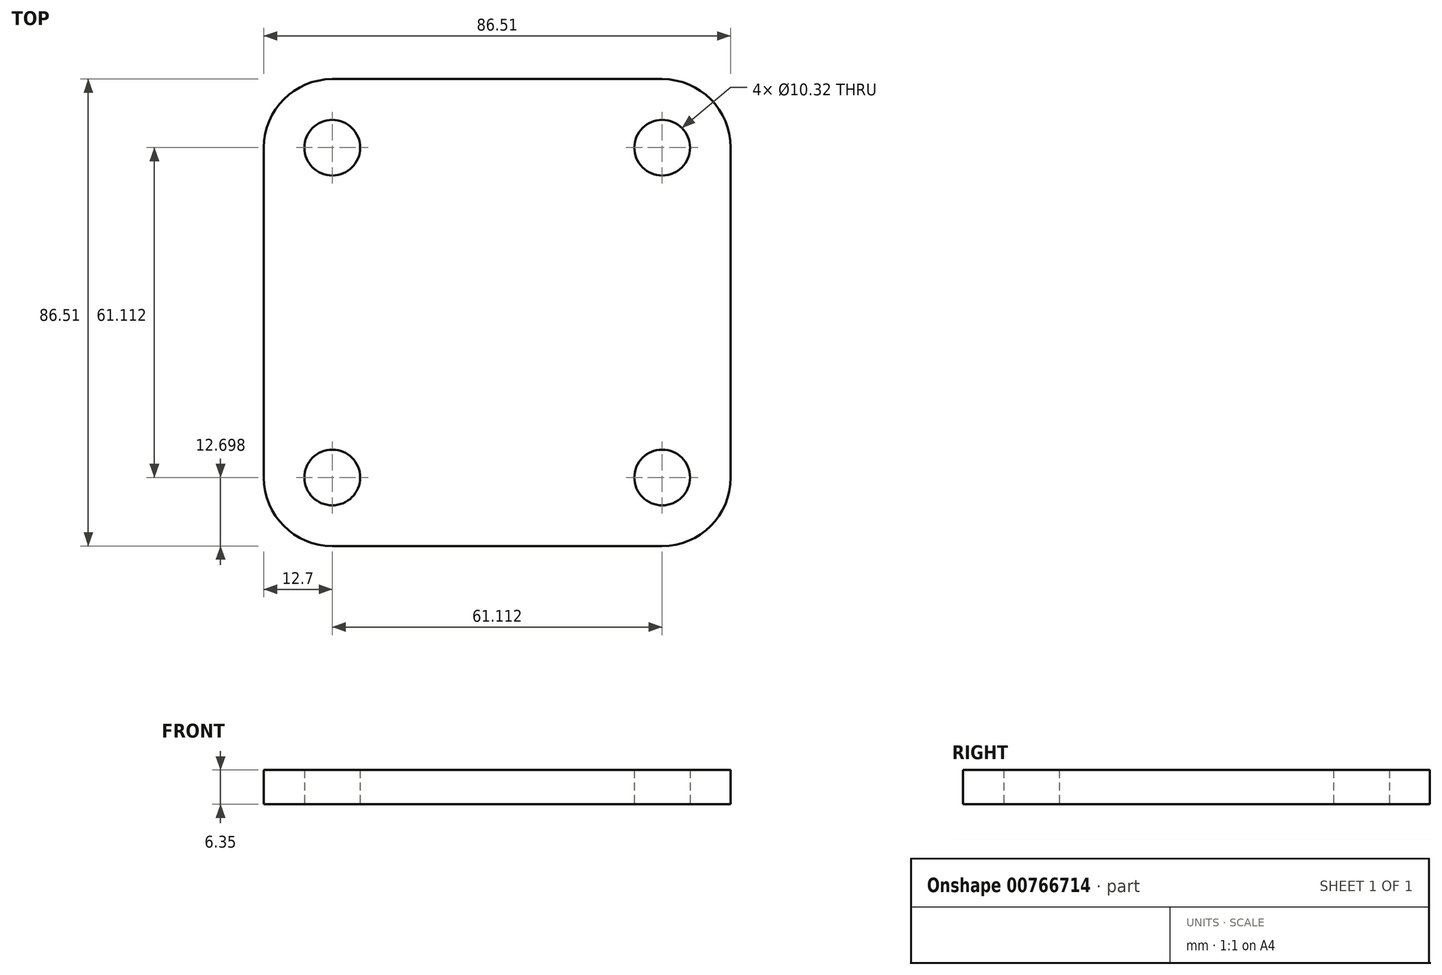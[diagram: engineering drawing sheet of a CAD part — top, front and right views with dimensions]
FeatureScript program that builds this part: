
annotation { "Feature Type Name" : "Feature", "Feature Type Description" : "" }
export const myFeature = defineFeature(function(context is Context, id is Id, definition is map)
    precondition{}
    {
        {
            var Q0;
            Q0=qCreatedBy(makeId("Top.planeOp"),FACE);
            var sketch = newSketch(context, id + "F0", { "sketchPlane" : qUnion([Q0])});
            skLineSegment(sketch, "E0.bottom", {"start": v(12.7, 0) * mm, "end": v(73.81, 0) * mm});
            skLineSegment(sketch, "E0.top", {"start": v(12.7, -86.51) * mm, "end": v(73.81, -86.51) * mm});
            skLineSegment(sketch, "E0.left", {"start": v(0, -12.7) * mm, "end": v(0, -73.81) * mm});
            skLineSegment(sketch, "E0.right", {"start": v(86.51, -12.7) * mm, "end": v(86.51, -73.81) * mm});
            skCircle(sketch, "E1", {"center": v(12.7, -12.7) * mm, "radius": 5.16 * mm});
            skCircle(sketch, "E2.0.1.0", {"center": v(12.7, -73.81) * mm, "radius": 5.16 * mm});
            skCircle(sketch, "E2.1.0.0", {"center": v(73.81, -12.7) * mm, "radius": 5.16 * mm});
            skCircle(sketch, "E2.1.1.0", {"center": v(73.81, -73.81) * mm, "radius": 5.16 * mm});
            skLineSegment(sketch, "E2.direction1", {"start": v(12.7, -12.7) * mm, "end": v(73.81, -12.7) * mm, "construction": true});
            skLineSegment(sketch, "E2.direction2", {"start": v(12.7, -12.7) * mm, "end": v(12.7, -73.81) * mm, "construction": true});
            skPoint(sketch, "E3.visualSharp", {"position": v(0, 0) * mm});
            skArc(sketch, "E3.filletArc", {"start": v(12.7, 0) * mm, "mid": v(3.72, -3.72) * mm, "end": v(0, -12.7) * mm});
            skPoint(sketch, "E4.visualSharp", {"position": v(86.51, 0) * mm});
            skArc(sketch, "E4.filletArc", {"start": v(86.51, -12.7) * mm, "mid": v(82.8, -3.72) * mm, "end": v(73.81, 0) * mm});
            skPoint(sketch, "E5.visualSharp", {"position": v(86.51, -86.51) * mm});
            skArc(sketch, "E5.filletArc", {"start": v(73.81, -86.51) * mm, "mid": v(82.8, -82.8) * mm, "end": v(86.51, -73.81) * mm});
            skPoint(sketch, "E6.visualSharp", {"position": v(0, -86.51) * mm});
            skArc(sketch, "E6.filletArc", {"start": v(0, -73.81) * mm, "mid": v(3.72, -82.8) * mm, "end": v(12.7, -86.51) * mm});
            skSolve(sketch);
        }
        {
            var Q0;
            Q0=makeQuery(id+"F0.imprint","IMPRINT",FACE,{"disambiguationData":[TD([[makeQuery(id+"F0.imprint","IMPRINT",EDGE,{"derivedFrom":sQuery(id+"F0.wireOp",EDGE,"E0.bottom")}),-1.0]])]});
            extrude(context, id + "F1", {"entities" : qUnion([Q0]), "depth" : 6.35 * mm, "offsetDistance" : 25.4 * mm});
        }
    });
